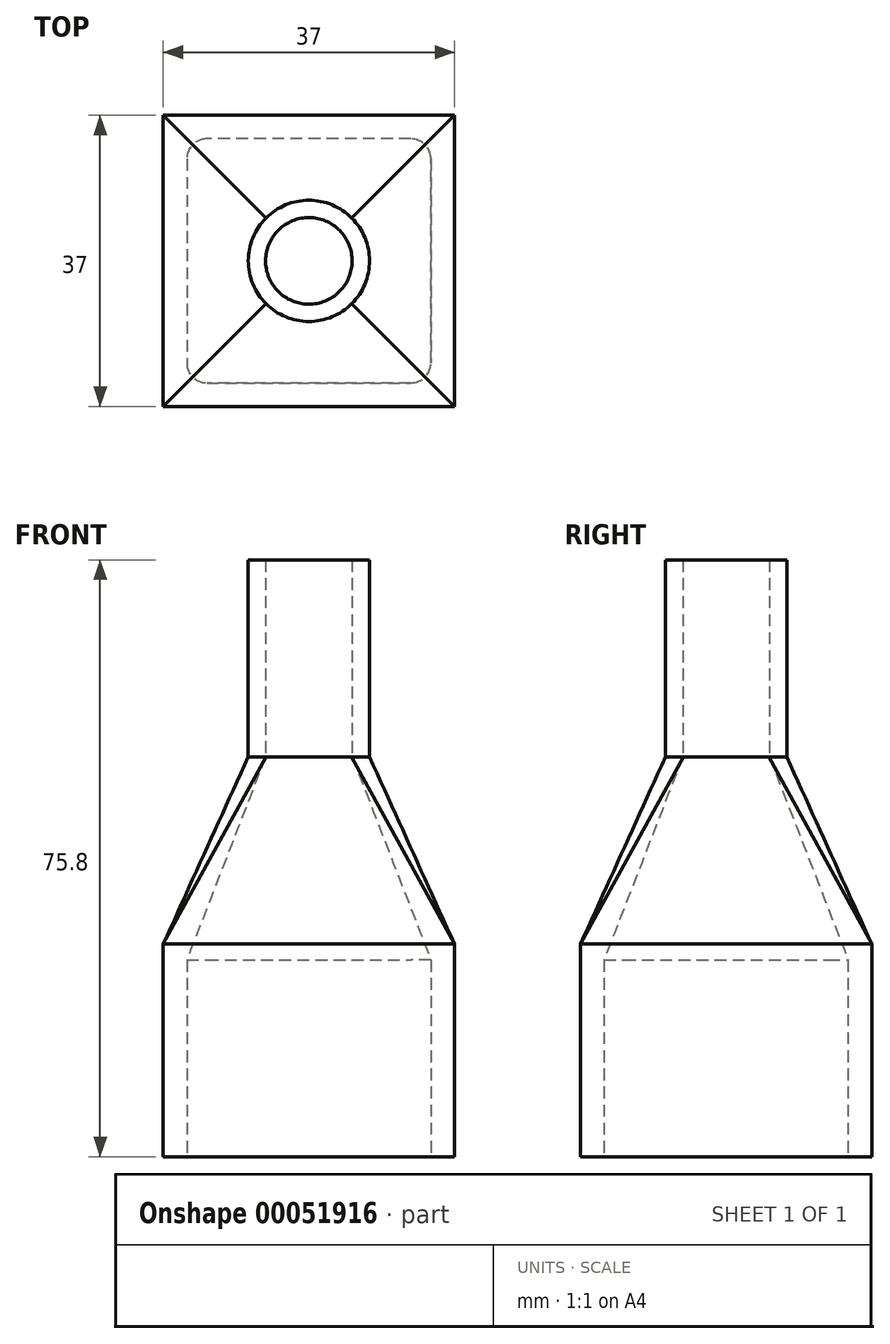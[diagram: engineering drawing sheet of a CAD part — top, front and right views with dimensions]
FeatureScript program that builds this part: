
annotation { "Feature Type Name" : "Feature", "Feature Type Description" : "" }
export const myFeature = defineFeature(function(context is Context, id is Id, definition is map)
    precondition{}
    {
        {
            var Q0;
            Q0=qCreatedBy(makeId("Top.planeOp"),FACE);
            var sketch = newSketch(context, id + "F0", { "sketchPlane" : qUnion([Q0])});
            skLineSegment(sketch, "E0.rect.bottom", {"start": v(12.96, 15.5) * mm, "end": v(-12.96, 15.5) * mm});
            skLineSegment(sketch, "E0.rect.top", {"start": v(12.96, -15.5) * mm, "end": v(-12.96, -15.5) * mm});
            skLineSegment(sketch, "E0.rect.left", {"start": v(15.5, 12.96) * mm, "end": v(15.5, -12.96) * mm});
            skLineSegment(sketch, "E0.rect.right", {"start": v(-15.5, 12.96) * mm, "end": v(-15.5, -12.96) * mm});
            skPoint(sketch, "E0.rect.middle", {"position": v(0, 0) * mm});
            skPoint(sketch, "E1.visualSharp", {"position": v(-15.5, 15.5) * mm});
            skArc(sketch, "E1.filletArc", {"start": v(-12.96, 15.5) * mm, "mid": v(-14.76, 14.76) * mm, "end": v(-15.5, 12.96) * mm});
            skPoint(sketch, "E2.visualSharp", {"position": v(15.5, 15.5) * mm});
            skArc(sketch, "E2.filletArc", {"start": v(15.5, 12.96) * mm, "mid": v(14.76, 14.76) * mm, "end": v(12.96, 15.5) * mm});
            skPoint(sketch, "E3.visualSharp", {"position": v(15.5, -15.5) * mm});
            skArc(sketch, "E3.filletArc", {"start": v(12.96, -15.5) * mm, "mid": v(14.76, -14.76) * mm, "end": v(15.5, -12.96) * mm});
            skPoint(sketch, "E4.visualSharp", {"position": v(-15.5, -15.5) * mm});
            skArc(sketch, "E4.filletArc", {"start": v(-15.5, -12.96) * mm, "mid": v(-14.76, -14.76) * mm, "end": v(-12.96, -15.5) * mm});
            skLineSegment(sketch, "E5.rect.bottom", {"start": v(18.5, 18.5) * mm, "end": v(-18.5, 18.5) * mm});
            skLineSegment(sketch, "E5.rect.top", {"start": v(18.5, -18.5) * mm, "end": v(-18.5, -18.5) * mm});
            skLineSegment(sketch, "E5.rect.left", {"start": v(18.5, 18.5) * mm, "end": v(18.5, -18.5) * mm});
            skLineSegment(sketch, "E5.rect.right", {"start": v(-18.5, 18.5) * mm, "end": v(-18.5, -18.5) * mm});
            skSolve(sketch);
        }
        {
            var Q0;
            Q0=makeQuery(id+"F0.imprint","IMPRINT",FACE,{"disambiguationData":[TD([[makeQuery(id+"F0.imprint","IMPRINT",EDGE,{"derivedFrom":sQuery(id+"F0.wireOp",EDGE,"E0.rect.bottom")}),-1.0]])]});
            extrude(context, id + "F1", {"entities" : qUnion([Q0]), "depth" : 25 * mm});
        }
        {
            var Q0;
            Q0=qCreatedBy(makeId("Top.planeOp"),FACE);
            cPlane(context, id + "F2", {"entities" : qUnion([Q0]), "cplaneType" : CPlaneType.OFFSET, "offset" : 50.8 * mm, "width" : 150 * mm, "height" : 150 * mm});
        }
        {
            var Q0;
            Q0=qCreatedBy(id+"F2.planeOp",FACE);
            var sketch = newSketch(context, id + "F3", { "sketchPlane" : qUnion([Q0])});
            skCircle(sketch, "E6", {"center": v(0, 0) * mm, "radius": 7.7 * mm});
            skSolve(sketch);
        }
        {
            var Q0;
            Q0=makeQuery(id+"F1.opExtrude","CAP_FACE",FACE,{"disambiguationData":[OSD([sQuery(id+"F0.wireOp",EDGE,"E0.rect.bottom"),sQuery(id+"F0.wireOp",EDGE,"E0.rect.top"),sQuery(id+"F0.wireOp",EDGE,"E0.rect.left"),sQuery(id+"F0.wireOp",EDGE,"E0.rect.right"),sQuery(id+"F0.wireOp",EDGE,"E1.filletArc"),sQuery(id+"F0.wireOp",EDGE,"E2.filletArc"),sQuery(id+"F0.wireOp",EDGE,"E3.filletArc"),sQuery(id+"F0.wireOp",EDGE,"E4.filletArc"),sQuery(id+"F0.wireOp",EDGE,"E5.rect.bottom"),sQuery(id+"F0.wireOp",EDGE,"E5.rect.top"),sQuery(id+"F0.wireOp",EDGE,"E5.rect.left"),sQuery(id+"F0.wireOp",EDGE,"E5.rect.right")])],"isStart":false});
            var sketch = newSketch(context, id + "F4", { "sketchPlane" : qUnion([Q0])});
            skLineSegment(sketch, "E7.rect.bottom", {"start": v(18.5, 18.5) * mm, "end": v(-18.5, 18.5) * mm});
            skLineSegment(sketch, "E7.rect.top", {"start": v(18.5, -18.5) * mm, "end": v(-18.5, -18.5) * mm});
            skLineSegment(sketch, "E7.rect.left", {"start": v(18.5, 18.5) * mm, "end": v(18.5, -18.5) * mm});
            skLineSegment(sketch, "E7.rect.right", {"start": v(-18.5, 18.5) * mm, "end": v(-18.5, -18.5) * mm});
            skPoint(sketch, "E7.rect.middle", {"position": v(0, 0) * mm});
            skSolve(sketch);
        }
        {
            var Q0;
            Q0 = qSketchRegion(id + "F4", true);
            extrude(context, id + "F5", {"entities" : qUnion([Q0]), "operationType" : NewBodyOperationType.ADD, "depth" : 2 * mm});
        }
        {
            var Q1;
            Q1=makeQuery(id+"F5.opExtrude","CAP_FACE",FACE,{"disambiguationData":[OSD([sQuery(id+"F4.wireOp",EDGE,"E7.rect.bottom"),sQuery(id+"F4.wireOp",EDGE,"E7.rect.top"),sQuery(id+"F4.wireOp",EDGE,"E7.rect.left"),sQuery(id+"F4.wireOp",EDGE,"E7.rect.right")])],"isStart":false});
            var Q2;
            Q2=makeQuery(id+"F3.imprint","IMPRINT",FACE,{"disambiguationData":[TD([[makeQuery(id+"F3.imprint","IMPRINT",EDGE,{"derivedFrom":sQuery(id+"F3.wireOp",EDGE,"E6")}),1.0]])]});
            loft(context, id + "F6", {"operationType" : NewBodyOperationType.ADD, "sheetProfilesArray" : [{ "sheetProfileEntities" : qUnion([Q1]) }, { "sheetProfileEntities" : qUnion([Q2]) }]});
        }
        {
            var Q0;
            Q0=makeQuery(id+"F6.opLoft","CAP_FACE",FACE,{"disambiguationData":[OSD([makeQuery(id+"F3.imprint","IMPRINT",FACE,{"disambiguationData":[TD([[makeQuery(id+"F3.imprint","IMPRINT",EDGE,{"derivedFrom":sQuery(id+"F3.wireOp",EDGE,"E6")}),1.0]])]})])],"isStart":true});
            var sketch = newSketch(context, id + "F7", { "sketchPlane" : qUnion([Q0])});
            skCircle(sketch, "E8", {"center": v(0, 0) * mm, "radius": 5.5 * mm});
            skSolve(sketch);
        }
        {
            var Q1;
            Q1=makeQuery(id+"F5.opExtrude","CAP_FACE",FACE,{"disambiguationData":[OSD([sQuery(id+"F4.wireOp",EDGE,"E7.rect.bottom"),sQuery(id+"F4.wireOp",EDGE,"E7.rect.top"),sQuery(id+"F4.wireOp",EDGE,"E7.rect.left"),sQuery(id+"F4.wireOp",EDGE,"E7.rect.right")])],"isStart":true});
            var Q2;
            Q2=makeQuery(id+"F7.imprint","IMPRINT",FACE,{"disambiguationData":[TD([[makeQuery(id+"F7.imprint","IMPRINT",EDGE,{"derivedFrom":sQuery(id+"F7.wireOp",EDGE,"E8")}),1.0]])]});
            loft(context, id + "F8", {"operationType" : NewBodyOperationType.REMOVE, "sheetProfilesArray" : [{ "sheetProfileEntities" : qUnion([Q1]) }, { "sheetProfileEntities" : qUnion([Q2]) }]});
        }
        {
            var Q0;
            Q0=makeQuery(id+"F6.opLoft","CAP_FACE",FACE,{"disambiguationData":[OSD([makeQuery(id+"F3.imprint","IMPRINT",FACE,{"disambiguationData":[TD([[makeQuery(id+"F3.imprint","IMPRINT",EDGE,{"derivedFrom":sQuery(id+"F3.wireOp",EDGE,"E6")}),1.0]])]})])],"isStart":true});
            extrude(context, id + "F9", {"entities" : qUnion([Q0]), "operationType" : NewBodyOperationType.ADD, "depth" : 25 * mm});
        }
    });
